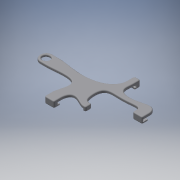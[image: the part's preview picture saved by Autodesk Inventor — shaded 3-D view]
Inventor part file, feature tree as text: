
AUTODESK INVENTOR PART (.ipt)
format: ipt  version: 2018 (Build 220112000, 112)  size: 417,792 bytes
history: native  units: mm
features: extrude x4, fillet x4, sketch x4, reference x2, other x2
ambient origin geometry x8: Origin, YZ Plane, XZ Plane, XY Plane, X Axis, Y Axis, Z Axis, Center Point
bodies: Solid1 (feature_tree)
feature tree (16):
  extrude  "Extrusion1"  Depth=6.0mm
  extrude  "Extrusion2"  Depth=3.0mm
  extrude  "Extrusion3"  Depth=3.0mm
  fillet  "Fillet1"  [1 undecoded]
  fillet  "Fillet2"  Radius=5.0mm
  fillet  "Fillet3"  Radius=6.0mm
  fillet  "Fillet4"  Radius=8.0mm
  extrude  "Extrusion4"  Depth=10.0mm
  sketch  "Sketch1"  dims[d0=20.0mm d1=6.0mm]
  reference  "Reference1"
  sketch  "Sketch2"  dims[d2=4.0mm d3=3.0mm]
  sketch  "Sketch3"  dims[d4=3.0mm d5=3.0mm d6=0.0mm d7=5.0mm d8=6.0mm d9=8.0mm]
  sketch  "Sketch4"  dims[d10=6.0mm d11=10.0mm d12=2.0mm d13=5.0mm d14=14.0mm d15=15.0mm d16=6.0mm d17=8.0mm d18=5.0mm d19=10.0mm d20=6.0mm d21=5.0mm d22=2.0mm d23=0.0mm d24=8.0mm d25=3.0mm d26=8.0mm d27=3.0mm d28=5.0mm d29=3.0mm d30=2.0mm d31=5.0mm d32=1.8mm d33=0.0mm d34=8.0mm d35=4.5mm d36=5.0mm d37=4.5mm d38=8.0mm d39=4.5mm d40=1.5mm d41=0.0mm d42=4.0mm d43=1.2mm d44=0.8mm d45=0.8mm d46=7.0mm d47=15.0mm d48=4.0mm d49=10.0mm d50=1.0mm d51=0.0mm]
  reference  "Reference2"
  other  "Assembly1"
  other  "PCB:1"
note: 1 required parameter value undecoded (feature->parameter linkage not recoverable at this tier; creation-order binding heuristic only, values carry confidence <= 0.55)
